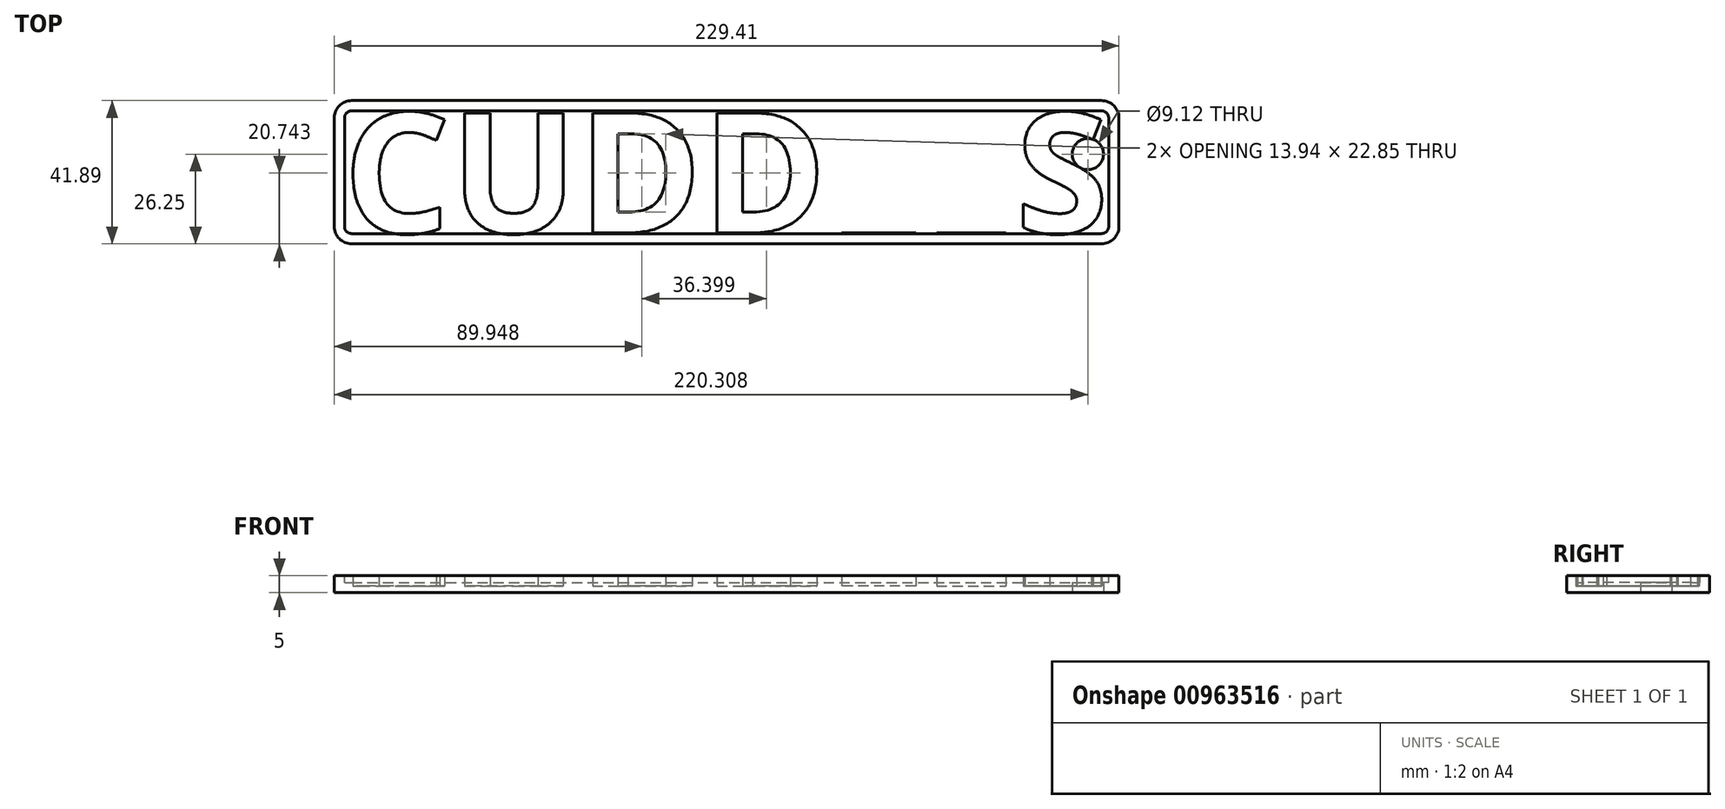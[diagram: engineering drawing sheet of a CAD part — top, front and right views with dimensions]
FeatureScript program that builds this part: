
annotation { "Feature Type Name" : "Feature", "Feature Type Description" : "" }
export const myFeature = defineFeature(function(context is Context, id is Id, definition is map)
    precondition{}
    {
        {
            var Q0;
            Q0=qCreatedBy(makeId("Top.planeOp"),FACE);
            var sketch = newSketch(context, id + "F0", { "sketchPlane" : qUnion([Q0])});
            skText(sketch, "E0", { "text": "CUDDLES", "fontName": "OpenSans-Bold.ttf"});
            skLineSegment(sketch, "E1.bottom", {"start": v(-117.8, -17.32) * mm, "end": v(107.18, -17.32) * mm});
            skLineSegment(sketch, "E1.top", {"start": v(-117.8, 18.1) * mm, "end": v(107.18, 18.1) * mm});
            skLineSegment(sketch, "E1.left", {"start": v(-117.8, -17.32) * mm, "end": v(-117.8, 18.1) * mm});
            skLineSegment(sketch, "E1.right", {"start": v(107.18, -17.32) * mm, "end": v(107.18, 18.1) * mm});
            const initialGuessF0  = {"E0": [-0.1178, -0.01732, 1, 0, 0.0354]};
            skSetInitialGuess(sketch, initialGuessF0);
            skSolve(sketch);
        }
        {
            var Q0;
            {var subQ0=sQuery(id+"F0.wireOp",EDGE,"E0.sketch_text.stroke-6");var subQ1=sQuery(id+"F0.wireOp",EDGE,"E0.sketch_text.stroke-5");var subQ2=makeQuery(id+"F0.imprint","INTERSECT",VERTEX,{"derivedFrom":[subQ1,subQ0]});Q0=makeQuery(id+"F0.imprint","IMPRINT",FACE,{"disambiguationData":[TD([[makeQuery(id+"F0.imprint","IMPRINT",EDGE,{"disambiguationData":[TD([[subQ2,1.0]])],"derivedFrom":subQ1}),-1.0]])]});}
            var Q1;
            {var subQ0=sQuery(id+"F0.wireOp",EDGE,"E0.sketch_text.stroke-11");var subQ1=sQuery(id+"F0.wireOp",EDGE,"E0.sketch_text.stroke-10");var subQ2=makeQuery(id+"F0.imprint","INTERSECT",VERTEX,{"derivedFrom":[subQ1,subQ0]});Q1=makeQuery(id+"F0.imprint","IMPRINT",FACE,{"disambiguationData":[TD([[makeQuery(id+"F0.imprint","IMPRINT",EDGE,{"disambiguationData":[TD([[subQ2,1.0]])],"derivedFrom":subQ1}),-1.0]])]});}
            var Q2;
            {var subQ0=sQuery(id+"F0.wireOp",EDGE,"E0.sketch_text.stroke-19");var subQ1=sQuery(id+"F0.wireOp",EDGE,"E0.sketch_text.stroke-18");var subQ2=makeQuery(id+"F0.imprint","INTERSECT",VERTEX,{"derivedFrom":[subQ1,subQ0]});Q2=makeQuery(id+"F0.imprint","IMPRINT",FACE,{"disambiguationData":[TD([[makeQuery(id+"F0.imprint","IMPRINT",EDGE,{"disambiguationData":[TD([[subQ2,1.0]])],"derivedFrom":subQ1}),-1.0]])]});}
            var Q3;
            {var subQ1=sQuery(id+"F0.wireOp",EDGE,"E0.sketch_text.stroke-54");Q3=makeQuery(id+"F0.imprint","IMPRINT",FACE,{"disambiguationData":[TD([[makeQuery(id+"F0.imprint","IMPRINT",EDGE,{"derivedFrom":subQ1}),-1.0]])]});}
            var Q4;
            {var subQ1=sQuery(id+"F0.wireOp",EDGE,"E0.sketch_text.stroke-61");Q4=makeQuery(id+"F0.imprint","IMPRINT",FACE,{"disambiguationData":[TD([[makeQuery(id+"F0.imprint","IMPRINT",EDGE,{"derivedFrom":subQ1}),-1.0]])]});}
            var Q5;
            {var subQ0=sQuery(id+"F0.wireOp",EDGE,"E0.sketch_text.stroke-74");var subQ1=sQuery(id+"F0.wireOp",EDGE,"E0.sketch_text.stroke-73");var subQ2=makeQuery(id+"F0.imprint","INTERSECT",VERTEX,{"derivedFrom":[subQ1,subQ0]});Q5=makeQuery(id+"F0.imprint","IMPRINT",FACE,{"disambiguationData":[TD([[makeQuery(id+"F0.imprint","IMPRINT",EDGE,{"disambiguationData":[TD([[subQ2,1.0]])],"derivedFrom":subQ1}),-1.0]])]});}
            var Q6;
            {var subQ0=sQuery(id+"F0.wireOp",EDGE,"E0.sketch_text.stroke-88");var subQ1=sQuery(id+"F0.wireOp",EDGE,"E0.sketch_text.stroke-87");var subQ2=makeQuery(id+"F0.imprint","INTERSECT",VERTEX,{"derivedFrom":[subQ1,subQ0]});Q6=makeQuery(id+"F0.imprint","IMPRINT",FACE,{"disambiguationData":[TD([[makeQuery(id+"F0.imprint","IMPRINT",EDGE,{"disambiguationData":[TD([[subQ2,1.0]])],"derivedFrom":subQ1}),-1.0]])]});}
            var Q7;
            Q7=makeQuery(id+"F0.imprint","IMPRINT",FACE,{"disambiguationData":[TD([[makeQuery(id+"F0.imprint","IMPRINT",EDGE,{"derivedFrom":sQuery(id+"F0.wireOp",EDGE,"E0.sketch_text.stroke-15")}),-1.0]])]});
            var Q8;
            Q8=makeQuery(id+"F0.imprint","IMPRINT",FACE,{"disambiguationData":[TD([[makeQuery(id+"F0.imprint","IMPRINT",EDGE,{"derivedFrom":sQuery(id+"F0.wireOp",EDGE,"E0.sketch_text.stroke-30")}),-1.0]])]});
            var Q9;
            Q9=makeQuery(id+"F0.imprint","IMPRINT",FACE,{"disambiguationData":[TD([[makeQuery(id+"F0.imprint","IMPRINT",EDGE,{"derivedFrom":sQuery(id+"F0.wireOp",EDGE,"E0.sketch_text.stroke-42")}),-1.0]])]});
            var Q10;
            {var subQ12=sQuery(id+"F0.wireOp",EDGE,"E0.sketch_text.stroke-72");Q10=makeQuery(id+"F0.imprint","IMPRINT",FACE,{"disambiguationData":[TD([[makeQuery(id+"F0.imprint","IMPRINT",EDGE,{"derivedFrom":subQ12}),-1.0]])]});}
            var Q11;
            Q11=makeQuery(id+"F0.imprint","IMPRINT",FACE,{"disambiguationData":[TD([[makeQuery(id+"F0.imprint","IMPRINT",EDGE,{"derivedFrom":sQuery(id+"F0.wireOp",EDGE,"E0.sketch_text.stroke-0")}),-1.0]])]});
            extrude(context, id + "F1", {"entities" : qUnion([Q0, Q1, Q2, Q3, Q4, Q5, Q6, Q7, Q8, Q9, Q10, Q11]), "depth" : 3 * mm, "offsetDistance" : 25.4 * mm});
        }
        {
            var Q0;
            Q0=makeQuery(id+"F1.opExtrude","CAP_FACE",FACE,{"disambiguationData":[OSD([sQuery(id+"F0.wireOp",EDGE,"E0.sketch_text.stroke-42"),sQuery(id+"F0.wireOp",EDGE,"E0.sketch_text.stroke-43"),sQuery(id+"F0.wireOp",EDGE,"E0.sketch_text.stroke-45"),sQuery(id+"F0.wireOp",EDGE,"E0.sketch_text.stroke-46"),sQuery(id+"F0.wireOp",EDGE,"E0.sketch_text.stroke-47"),sQuery(id+"F0.wireOp",EDGE,"E0.sketch_text.stroke-48"),sQuery(id+"F0.wireOp",EDGE,"E0.sketch_text.stroke-49"),sQuery(id+"F0.wireOp",EDGE,"E0.sketch_text.stroke-50"),sQuery(id+"F0.wireOp",EDGE,"E0.sketch_text.stroke-51"),sQuery(id+"F0.wireOp",EDGE,"E0.sketch_text.stroke-52"),sQuery(id+"F0.wireOp",EDGE,"E0.sketch_text.stroke-53"),sQuery(id+"F0.wireOp",EDGE,"E1.bottom")])],"isStart":true});
            var sketch = newSketch(context, id + "F2", { "sketchPlane" : qUnion([Q0])});
            skLineSegment(sketch, "E2.bottom", {"start": v(-120.42, -21.4) * mm, "end": v(108.99, -21.4) * mm});
            skLineSegment(sketch, "E2.top", {"start": v(-120.42, 20.49) * mm, "end": v(108.99, 20.49) * mm});
            skLineSegment(sketch, "E2.left", {"start": v(-120.42, -21.4) * mm, "end": v(-120.42, 20.49) * mm});
            skLineSegment(sketch, "E2.right", {"start": v(108.99, -21.4) * mm, "end": v(108.99, 20.49) * mm});
            skSolve(sketch);
        }
        {
            var Q0;
            Q0=makeQuery(id+"F2.imprint","IMPRINT",FACE,{"disambiguationData":[TD([[makeQuery(id+"F2.imprint","IMPRINT",EDGE,{"derivedFrom":sQuery(id+"F2.wireOp",EDGE,"E2.bottom")}),1.0]])]});
            var Q1;
            Q1=makeQuery(id+"F2.imprint","IMPRINT",FACE,{"disambiguationData":[TD([[makeQuery(id+"F2.imprint","IMPRINT",EDGE,{"derivedFrom":makeQuery(id+"F1.opExtrude","CAP_EDGE",EDGE,{"disambiguationData":[OSD([sQuery(id+"F0.wireOp",EDGE,"E0.sketch_text.stroke-42")])],"isStart":true})}),1.0]])]});
            var Q2;
            Q2=makeQuery(id+"F2.imprint","IMPRINT",FACE,{"disambiguationData":[TD([[makeQuery(id+"F2.imprint","IMPRINT",EDGE,{"derivedFrom":makeQuery(id+"F1.opExtrude","CAP_EDGE",EDGE,{"disambiguationData":[OSD([sQuery(id+"F0.wireOp",EDGE,"E0.sketch_text.stroke-49")])],"isStart":true})}),-1.0]])]});
            extrude(context, id + "F3", {"entities" : qUnion([Q0, Q1, Q2]), "depth" : 2 * mm, "offsetDistance" : 25.4 * mm, "hasSecondDirection" : true, "secondDirectionOppositeDirection" : true, "secondDirectionDepth" : 3 * mm});
        }
        {
            var Q0;
            Q0=makeQuery(id+"F3.opExtrude","SWEPT_EDGE",EDGE,{"disambiguationData":[OSD([sQuery(id+"F2.wireOp",EDGE,"E2.bottom"),sQuery(id+"F2.wireOp",EDGE,"E2.left")])]});
            var Q1;
            Q1=makeQuery(id+"F3.opExtrude","SWEPT_EDGE",EDGE,{"disambiguationData":[OSD([sQuery(id+"F2.wireOp",EDGE,"E2.top"),sQuery(id+"F2.wireOp",EDGE,"E2.left")])]});
            var Q2;
            Q2=makeQuery(id+"F3.opExtrude","SWEPT_EDGE",EDGE,{"disambiguationData":[OSD([sQuery(id+"F2.wireOp",EDGE,"E2.top"),sQuery(id+"F2.wireOp",EDGE,"E2.right")])]});
            var Q3;
            Q3=makeQuery(id+"F3.opExtrude","SWEPT_EDGE",EDGE,{"disambiguationData":[OSD([sQuery(id+"F2.wireOp",EDGE,"E2.bottom"),sQuery(id+"F2.wireOp",EDGE,"E2.right")])]});
            fillet(context, id + "F4", {"entities" : qUnion([Q0, Q1, Q2, Q3]), "radius" : 5.08 * mm, "tangentPropagation" : true, "allowEdgeOverflow" : false});
        }
        {
            var Q0;
            Q0=makeQuery(id+"F3.opExtrude","CAP_FACE",FACE,{"disambiguationData":[OSD([sQuery(id+"F2.wireOp",EDGE,"E2.bottom"),sQuery(id+"F2.wireOp",EDGE,"E2.top"),sQuery(id+"F2.wireOp",EDGE,"E2.left"),sQuery(id+"F2.wireOp",EDGE,"E2.right")])],"isStart":true});
            shell(context, id + "F5", {"entities" : qUnion([Q0]), "thickness" : 3 * mm});
        }
        {
            var Q0;
            Q0=makeQuery(id+"F5.opShell","OFFSET_FACE",FACE,{"disambiguationData":[OSD([sQuery(id+"F2.wireOp",EDGE,"E2.bottom"),sQuery(id+"F2.wireOp",EDGE,"E2.top"),sQuery(id+"F2.wireOp",EDGE,"E2.left"),sQuery(id+"F2.wireOp",EDGE,"E2.right")])]});
            var sketch = newSketch(context, id + "F6", { "sketchPlane" : qUnion([Q0])});
            skCircle(sketch, "E3", {"center": v(99.89, 5.76) * mm, "radius": 4.56 * mm});
            skSolve(sketch);
        }
        {
            var Q0;
            Q0=makeQuery(id+"F6.imprint","IMPRINT",FACE,{"disambiguationData":[TD([[makeQuery(id+"F6.imprint","IMPRINT",EDGE,{"derivedFrom":sQuery(id+"F6.wireOp",EDGE,"E3")}),1.0]])]});
            extrude(context, id + "F7", {"entities" : qUnion([Q0]), "operationType" : NewBodyOperationType.REMOVE, "endBound" : BoundingType.THROUGH_ALL, "depth" : 25.4 * mm, "offsetDistance" : 25.4 * mm, "hasSecondDirection" : true, "secondDirectionBound" : SecondDirectionBoundingType.THROUGH_ALL, "secondDirectionOppositeDirection" : true, "secondDirectionDepth" : 25.4 * mm});
        }
    });
